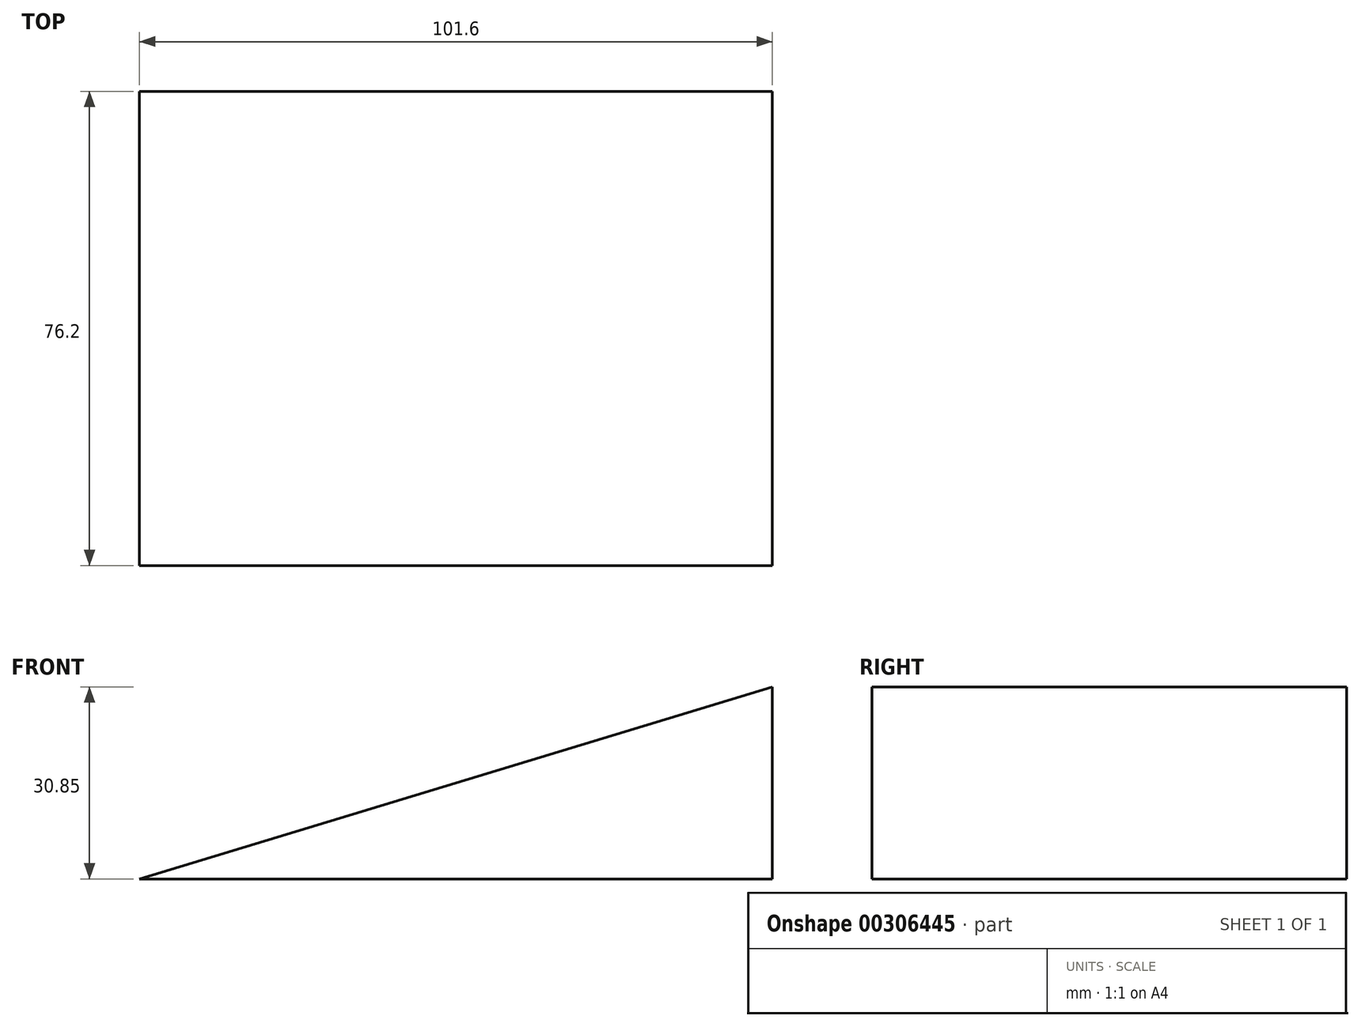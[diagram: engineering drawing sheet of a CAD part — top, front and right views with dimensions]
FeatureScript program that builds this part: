
annotation { "Feature Type Name" : "Feature", "Feature Type Description" : "" }
export const myFeature = defineFeature(function(context is Context, id is Id, definition is map)
    precondition{}
    {
        {
            var Q0;
            Q0=qCreatedBy(makeId("Front.planeOp"),FACE);
            var sketch = newSketch(context, id + "F0", { "sketchPlane" : qUnion([Q0])});
            skLineSegment(sketch, "E0", {"start": v(0, 0) * mm, "end": v(-101.6, 0) * mm});
            skLineSegment(sketch, "E1", {"start": v(-101.6, 0) * mm, "end": v(0, 30.85) * mm});
            skLineSegment(sketch, "E2", {"start": v(0, 30.85) * mm, "end": v(0, 0) * mm});
            skSolve(sketch);
        }
        {
            var Q0;
            Q0 = qSketchRegion(id + "F0", true);
            extrude(context, id + "F1", {"entities" : qUnion([Q0]), "depth" : 76.2 * mm});
        }
    });
